# Revit family: CSensor-Lutron-Dimmer_and_Switch-Vive_Maestro_MRF2S-8SS
name_source: partatom
category: Lighting Devices
units: mm (PartAtom-declared; Revit-internal decimal feet)

## family parameters
Cut with Voids When Loaded = No
Host = Face
Maintain Annotation Orientation = No
OmniClass Number = 23.85.80.11.27
OmniClass Title = Lighting Controls
Part Type = Normal
Room Calculation Point = No
Round Connector Dimension = Use Diameter
Shared = No

## types (1)
- MRF2S-8SS-XX
    Apparent Load = 0 VA
    Assembly Code = D5030800
    Cost = 0 $
    Coverage = 2827 SF
    Coverage Area = 360˚ coverage from 71 ft (22 m) RF Coverage, 400 sqft Sensor Coverage
    Coverage Radius = 30' - 0"
    Coverage Range = RF Coverage 30' Radius, Sensor Coverage 20 'x 20'
    Default Elevation = 0' - 0"
    Depth = 0' - 0 5/16"
    Description = Occupancy / vacancy single-pole/ multi-location sensor dimmer
    Dimmer = Yes
    Finish = Plastic - Lutron - White
    Instruction Sheet Link = https://www.lutron.com
    Keynote = Division 11
    Length = 0' - 4 11/16"
    Load Classification = Other
    Manufacturer = Lutron Electronics Co., Inc
    Manufacturer Fax Number = 610-282-1243
    Maximum Operating Temperature = 104 °F
    Model = MRF2S-8SS-XX
    Performance URL = http://www.lutron.com
    Product Documentation Link = https://www.lutron.com
    Product Name = Maestro RF 0–10 V Sensor Dimmer/ RF Sensor Switch
    Product Page URL = https://commercial.lutron.com
    Sensor Material = Plastic - Lutron - White
    Sensor Type = Occupancy/Vacancy
    Series = Vive Maestro Series
    Switch = No
    Type Comments = -
    URL = http://www.lutron.com
    Version = 2021 - v1.0a
    Video Link = https://www.youtube.com
    Voltage = 120 V
    Voltage Comments = 120/277 V
    Warranty URL = http://www.lutron.com
    Width = 0' - 2 15/16"

## geometry (parser evidence)
native form markers: Blend x4, Sweep x4
no freeform markers — native parametric forms only
